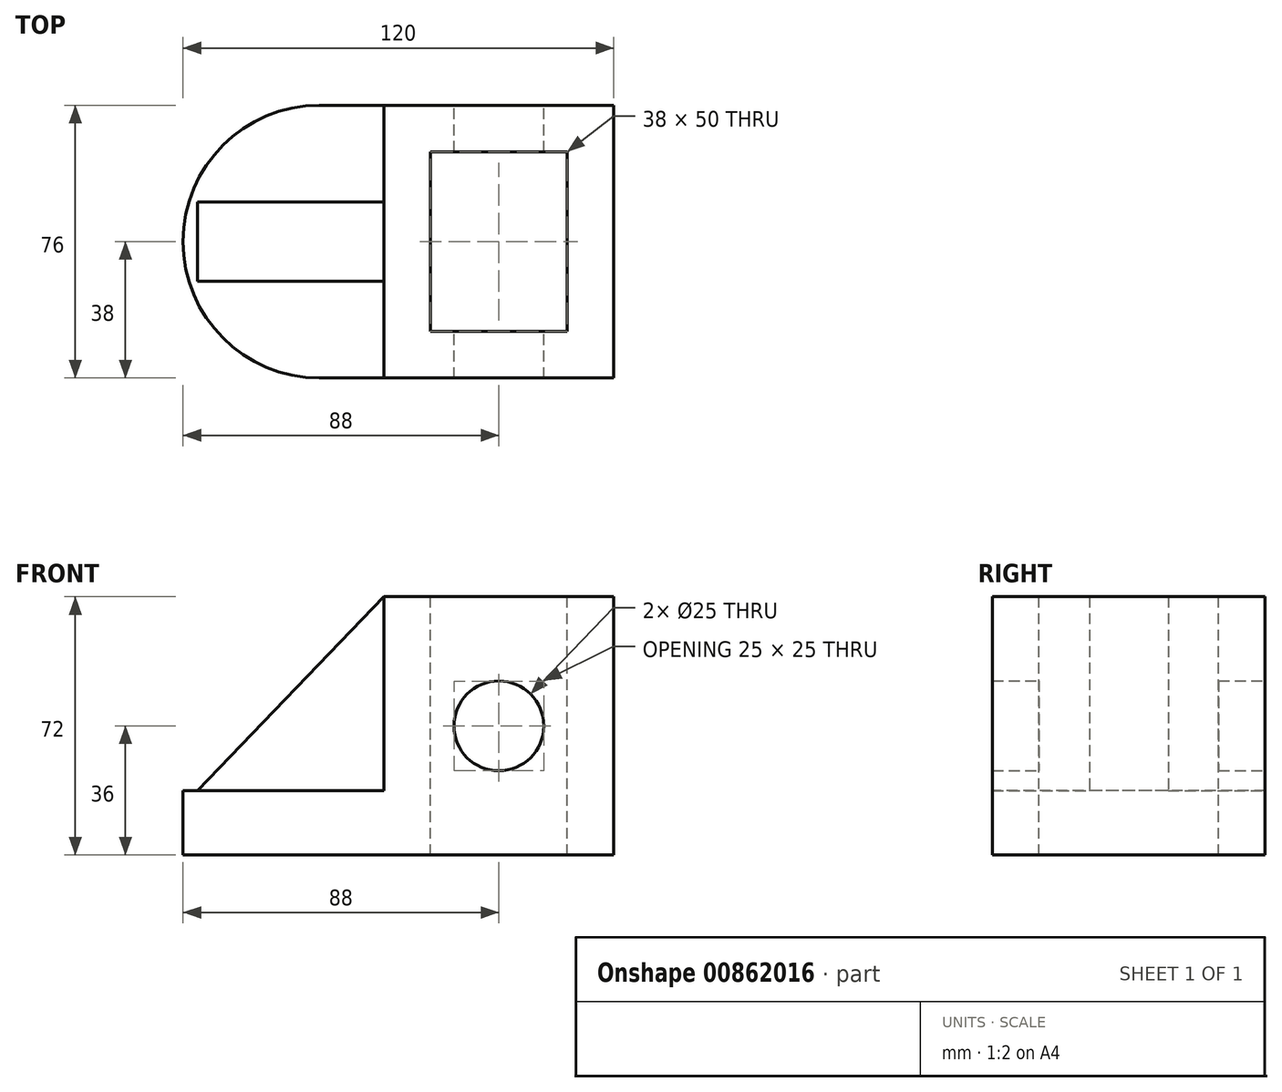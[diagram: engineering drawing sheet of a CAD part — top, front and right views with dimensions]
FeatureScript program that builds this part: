
annotation { "Feature Type Name" : "Feature", "Feature Type Description" : "" }
export const myFeature = defineFeature(function(context is Context, id is Id, definition is map)
    precondition{}
    {
        {
            var Q0;
            Q0=qCreatedBy(makeId("Front.planeOp"),FACE);
            var sketch = newSketch(context, id + "F0", { "sketchPlane" : qUnion([Q0])});
            skLineSegment(sketch, "E0", {"start": v(0, 0) * mm, "end": v(120, 0) * mm});
            skLineSegment(sketch, "E1", {"start": v(120, 0) * mm, "end": v(120, 72) * mm});
            skLineSegment(sketch, "E2", {"start": v(120, 72) * mm, "end": v(56, 72) * mm});
            skLineSegment(sketch, "E3", {"start": v(56, 72) * mm, "end": v(56, 18) * mm});
            skLineSegment(sketch, "E4", {"start": v(56, 18) * mm, "end": v(0, 18) * mm});
            skLineSegment(sketch, "E5", {"start": v(0, 0) * mm, "end": v(0, 18) * mm});
            skCircle(sketch, "E6", {"center": v(88, 36) * mm, "radius": 12.5 * mm});
            skPoint(sketch, "E6.centerSnap0", {"position": v(88, 72) * mm});
            skPoint(sketch, "E6.centerSnap1", {"position": v(120, 36) * mm});
            skSolve(sketch);
        }
        {
            var Q0;
            Q0=makeQuery(id+"F0.imprint","IMPRINT",FACE,{"disambiguationData":[TD([[makeQuery(id+"F0.imprint","IMPRINT",EDGE,{"derivedFrom":sQuery(id+"F0.wireOp",EDGE,"E0")}),1.0]])]});
            extrude(context, id + "F1", {"entities" : qUnion([Q0]), "depth" : 76 * mm, "offsetDistance" : 25 * mm});
        }
        {
            var Q0;
            Q0=makeQuery(id+"F1.opExtrude","SWEPT_FACE",FACE,{"disambiguationData":[OSD([sQuery(id+"F0.wireOp",EDGE,"E2")])]});
            var sketch = newSketch(context, id + "F2", { "sketchPlane" : qUnion([Q0])});
            skLineSegment(sketch, "E7.bottom", {"start": v(107, -13) * mm, "end": v(69, -13) * mm});
            skLineSegment(sketch, "E7.top", {"start": v(107, -63) * mm, "end": v(69, -63) * mm});
            skLineSegment(sketch, "E7.left", {"start": v(107, -13) * mm, "end": v(107, -63) * mm});
            skLineSegment(sketch, "E7.right", {"start": v(69, -13) * mm, "end": v(69, -63) * mm});
            skSolve(sketch);
        }
        {
            var Q0;
            Q0=makeQuery(id+"F2.imprint","IMPRINT",FACE,{"disambiguationData":[TD([[makeQuery(id+"F2.imprint","IMPRINT",EDGE,{"derivedFrom":sQuery(id+"F2.wireOp",EDGE,"E7.bottom")}),1.0]])]});
            extrude(context, id + "F3", {"entities" : qUnion([Q0]), "operationType" : NewBodyOperationType.REMOVE, "oppositeDirection" : true, "depth" : 124 * mm, "offsetDistance" : 25 * mm});
        }
        {
            var Q0;
            Q0=makeQuery(id+"F1.opExtrude","SWEPT_FACE",FACE,{"disambiguationData":[OSD([sQuery(id+"F0.wireOp",EDGE,"E4")])]});
            var sketch = newSketch(context, id + "F4", { "sketchPlane" : qUnion([Q0])});
            skArc(sketch, "E8", {"start": v(38, 0) * mm, "mid": v(0, -38) * mm, "end": v(38, -76) * mm});
            skSolve(sketch);
        }
        {
            var Q0;
            {var subQ0=sQuery(id+"F4.wireOp",EDGE,"E8");var subQ1=sQuery(id+"F0.wireOp",EDGE,"E4");var subQ2=makeQuery(id+"F1.opExtrude","CAP_EDGE",EDGE,{"disambiguationData":[OSD([subQ1])],"isStart":true});var subQ3=makeQuery(id+"F4.imprint","INTERSECT",VERTEX,{"derivedFrom":[subQ2,subQ0]});Q0=makeQuery(id+"F4.imprint","IMPRINT",FACE,{"disambiguationData":[TD([[makeQuery(id+"F4.imprint","IMPRINT",EDGE,{"disambiguationData":[TD([[subQ3,-1.0]])],"derivedFrom":subQ0}),-1.0]])]});}
            var Q1;
            {var subQ0=sQuery(id+"F4.wireOp",EDGE,"E8");var subQ1=sQuery(id+"F0.wireOp",EDGE,"E4");var subQ2=makeQuery(id+"F1.opExtrude","CAP_EDGE",EDGE,{"disambiguationData":[OSD([subQ1])],"isStart":false});var subQ3=makeQuery(id+"F4.imprint","INTERSECT",VERTEX,{"derivedFrom":[subQ2,subQ0]});Q1=makeQuery(id+"F4.imprint","IMPRINT",FACE,{"disambiguationData":[TD([[makeQuery(id+"F4.imprint","IMPRINT",EDGE,{"disambiguationData":[TD([[subQ3,1.0]])],"derivedFrom":subQ0}),-1.0]])]});}
            extrude(context, id + "F5", {"entities" : qUnion([Q0, Q1]), "operationType" : NewBodyOperationType.REMOVE, "oppositeDirection" : true, "depth" : 125.4 * mm, "offsetDistance" : 25 * mm});
        }
        {
            var Q0;
            Q0=makeQuery(id+"F1.opExtrude","SWEPT_FACE",FACE,{"disambiguationData":[OSD([sQuery(id+"F0.wireOp",EDGE,"E4")])]});
            var sketch = newSketch(context, id + "F6", { "sketchPlane" : qUnion([Q0])});
            skLineSegment(sketch, "E9", {"start": v(56, -38) * mm, "end": v(56, -27) * mm});
            skLineSegment(sketch, "E10", {"start": v(56, -38) * mm, "end": v(56, -49) * mm});
            skLineSegment(sketch, "E11", {"start": v(56, -49) * mm, "end": v(4, -49) * mm});
            skLineSegment(sketch, "E12", {"start": v(56, -27) * mm, "end": v(4, -27) * mm});
            skLineSegment(sketch, "E13", {"start": v(4, -27) * mm, "end": v(4, -49) * mm});
            skSolve(sketch);
        }
        {
            var Q0;
            Q0=makeQuery(id+"F6.imprint","IMPRINT",FACE,{"disambiguationData":[TD([[makeQuery(id+"F6.imprint","IMPRINT",EDGE,{"derivedFrom":sQuery(id+"F6.wireOp",EDGE,"E9")}),1.0]])]});
            extrude(context, id + "F7", {"entities" : qUnion([Q0]), "operationType" : NewBodyOperationType.ADD, "depth" : 54 * mm, "offsetDistance" : 25 * mm});
        }
        {
            var Q0;
            Q0=makeQuery(id+"F7.opExtrude","SWEPT_FACE",FACE,{"disambiguationData":[OSD([sQuery(id+"F6.wireOp",EDGE,"E11")])]});
            var sketch = newSketch(context, id + "F8", { "sketchPlane" : qUnion([Q0])});
            skLineSegment(sketch, "E14", {"start": v(4, 18) * mm, "end": v(56, 72) * mm});
            skLineSegment(sketch, "E15", {"start": v(56, 72) * mm, "end": v(62.73, 66.05) * mm});
            skLineSegment(sketch, "E16", {"start": v(62.73, 66.05) * mm, "end": v(10.74, 12.06) * mm});
            skSolve(sketch);
        }
        {
            var Q0;
            Q0=makeQuery(id+"F8.imprint","IMPRINT",FACE,{"disambiguationData":[TD([[makeQuery(id+"F8.imprint","IMPRINT",EDGE,{"derivedFrom":sQuery(id+"F8.wireOp",EDGE,"E14")}),1.0]])]});
            extrude(context, id + "F9", {"entities" : qUnion([Q0]), "operationType" : NewBodyOperationType.REMOVE, "oppositeDirection" : true, "depth" : 25 * mm, "offsetDistance" : 25 * mm});
        }
    });
